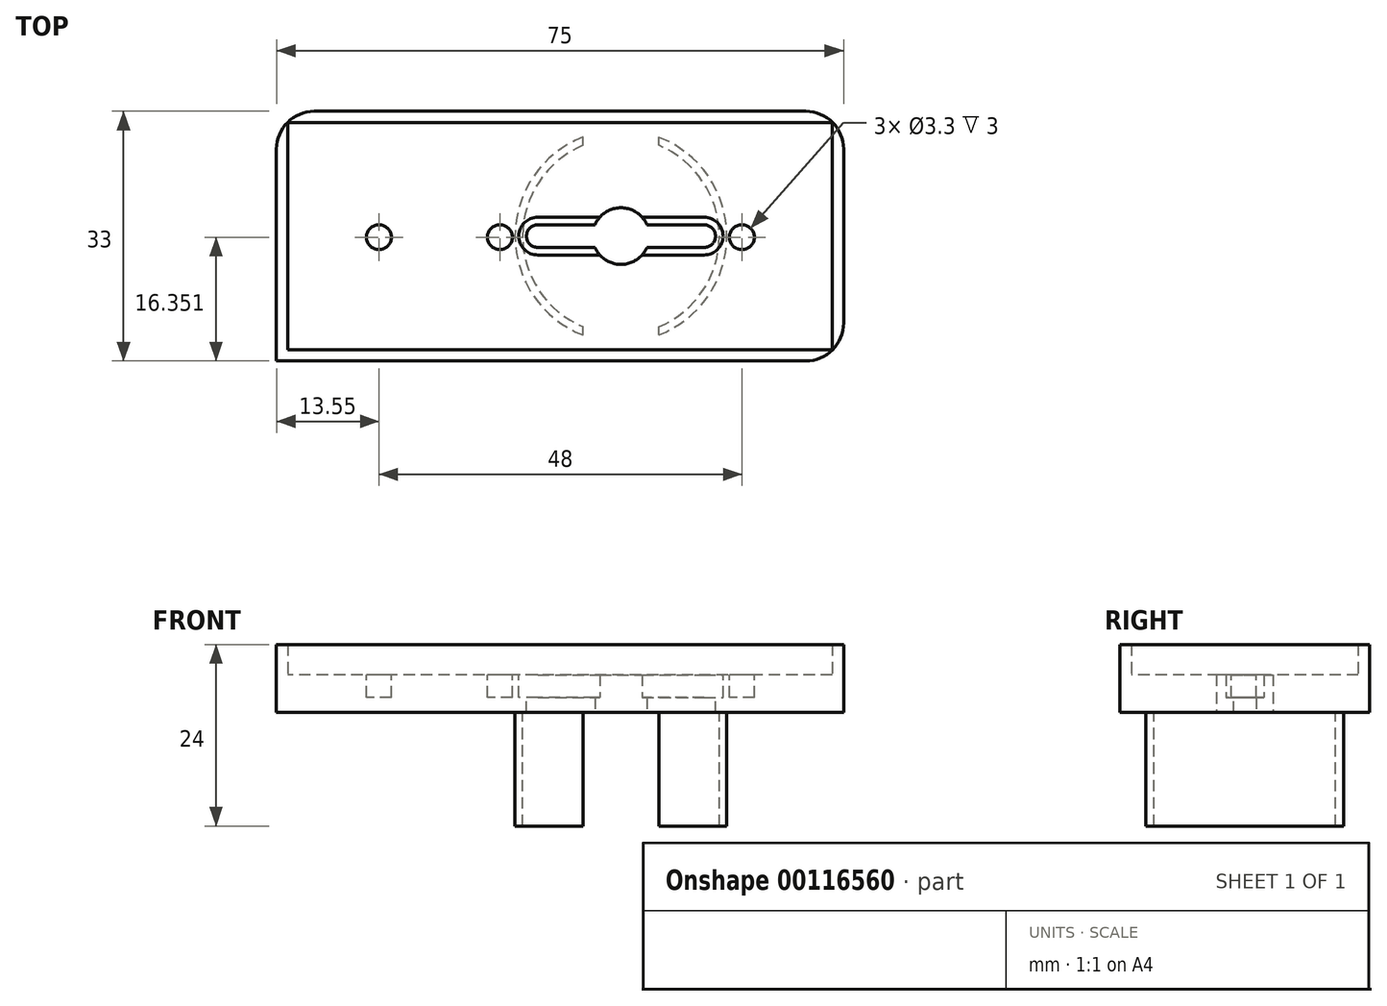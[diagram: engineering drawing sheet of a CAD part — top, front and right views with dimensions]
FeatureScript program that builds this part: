
annotation { "Feature Type Name" : "Feature", "Feature Type Description" : "" }
export const myFeature = defineFeature(function(context is Context, id is Id, definition is map)
    precondition{}
    {
        {
            var Q0;
            Q0=qCreatedBy(makeId("Top.planeOp"),FACE);
            var sketch = newSketch(context, id + "F0", { "sketchPlane" : qUnion([Q0])});
            skLineSegment(sketch, "E0.bottom", {"start": v(32.45, 18.12) * mm, "end": v(-32.55, 18.12) * mm});
            skLineSegment(sketch, "E0.top", {"start": v(32.45, -14.88) * mm, "end": v(-32.55, -14.88) * mm});
            skLineSegment(sketch, "E0.left", {"start": v(37.45, 13.12) * mm, "end": v(37.45, -9.88) * mm});
            skLineSegment(sketch, "E0.right", {"start": v(-37.55, 13.12) * mm, "end": v(-37.55, -9.88) * mm});
            skPoint(sketch, "E0.middle", {"position": v(-0.05, 1.62) * mm});
            skLineSegment(sketch, "E1.0", {"start": v(-36.05, 16.62) * mm, "end": v(-36.05, -13.38) * mm});
            skLineSegment(sketch, "E1.1", {"start": v(35.95, 16.62) * mm, "end": v(-36.05, 16.62) * mm});
            skLineSegment(sketch, "E1.2", {"start": v(35.95, 16.62) * mm, "end": v(35.95, -13.38) * mm});
            skLineSegment(sketch, "E1.3", {"start": v(35.95, -13.38) * mm, "end": v(-36.05, -13.38) * mm});
            skPoint(sketch, "E2.visualSharp", {"position": v(-37.55, -14.88) * mm});
            skPoint(sketch, "E3.visualSharp", {"position": v(37.45, -14.88) * mm});
            skArc(sketch, "E3.filletArc", {"start": v(32.45, -14.88) * mm, "mid": v(35.98, -13.42) * mm, "end": v(37.45, -9.88) * mm});
            skPoint(sketch, "E4.visualSharp", {"position": v(37.45, 18.12) * mm});
            skArc(sketch, "E4.filletArc", {"start": v(37.45, 13.12) * mm, "mid": v(35.98, 16.65) * mm, "end": v(32.45, 18.12) * mm});
            skPoint(sketch, "E5.visualSharp", {"position": v(-37.55, 18.12) * mm});
            skArc(sketch, "E5.filletArc", {"start": v(-32.55, 18.12) * mm, "mid": v(-36.09, 16.65) * mm, "end": v(-37.55, 13.12) * mm});
            skLineSegment(sketch, "E6", {"start": v(-32.55, -14.88) * mm, "end": v(-37.55, -14.88) * mm});
            skLineSegment(sketch, "E7", {"start": v(-37.55, -9.88) * mm, "end": v(-37.55, -14.88) * mm});
            skSolve(sketch);
        }
        {
            var Q0;
            Q0 = qSketchRegion(id + "F0", true);
            extrude(context, id + "F1", {"entities" : qUnion([Q0]), "depth" : 4 * mm});
        }
        {
            var Q0;
            Q0=makeQuery(id+"F1.opExtrude","CAP_FACE",FACE,{"disambiguationData":[OSD([sQuery(id+"F0.wireOp",EDGE,"E0.bottom"),sQuery(id+"F0.wireOp",EDGE,"E0.top"),sQuery(id+"F0.wireOp",EDGE,"E0.left"),sQuery(id+"F0.wireOp",EDGE,"E0.right"),sQuery(id+"F0.wireOp",EDGE,"E1.0"),sQuery(id+"F0.wireOp",EDGE,"E1.1"),sQuery(id+"F0.wireOp",EDGE,"E1.2"),sQuery(id+"F0.wireOp",EDGE,"E1.3"),sQuery(id+"F0.wireOp",EDGE,"E2.filletArc"),sQuery(id+"F0.wireOp",EDGE,"E3.filletArc"),sQuery(id+"F0.wireOp",EDGE,"E4.filletArc")])],"isStart":true});
            var sketch = newSketch(context, id + "F2", { "sketchPlane" : qUnion([Q0])});
            skLineSegment(sketch, "E8.bottom", {"start": v(-37.55, 14.88) * mm, "end": v(32.45, 14.88) * mm});
            skLineSegment(sketch, "E8.top", {"start": v(-32.55, -18.12) * mm, "end": v(32.45, -18.12) * mm});
            skLineSegment(sketch, "E8.left", {"start": v(-37.55, 14.88) * mm, "end": v(-37.55, -13.12) * mm});
            skLineSegment(sketch, "E8.right", {"start": v(37.45, 9.88) * mm, "end": v(37.45, -13.12) * mm});
            skPoint(sketch, "E9.visualSharp", {"position": v(-37.55, -18.12) * mm});
            skArc(sketch, "E9.filletArc", {"start": v(-37.55, -13.12) * mm, "mid": v(-36.09, -16.65) * mm, "end": v(-32.55, -18.12) * mm});
            skPoint(sketch, "E10.visualSharp", {"position": v(37.45, -18.12) * mm});
            skArc(sketch, "E10.filletArc", {"start": v(32.45, -18.12) * mm, "mid": v(35.98, -16.65) * mm, "end": v(37.45, -13.12) * mm});
            skPoint(sketch, "E11.visualSharp", {"position": v(37.45, 14.88) * mm});
            skArc(sketch, "E11.filletArc", {"start": v(37.45, 9.88) * mm, "mid": v(35.98, 13.42) * mm, "end": v(32.45, 14.88) * mm});
            skSolve(sketch);
        }
        {
            var Q0;
            Q0 = qSketchRegion(id + "F2", true);
            extrude(context, id + "F3", {"entities" : qUnion([Q0]), "operationType" : NewBodyOperationType.ADD, "depth" : 5 * mm});
        }
        {
            var Q0;
            Q0=makeQuery(id+"F3.opExtrude","CAP_FACE",FACE,{"disambiguationData":[OSD([sQuery(id+"F2.wireOp",EDGE,"E8.bottom"),sQuery(id+"F2.wireOp",EDGE,"E8.top"),sQuery(id+"F2.wireOp",EDGE,"E8.left"),sQuery(id+"F2.wireOp",EDGE,"E8.right"),sQuery(id+"F2.wireOp",EDGE,"E9.filletArc"),sQuery(id+"F2.wireOp",EDGE,"E10.filletArc"),sQuery(id+"F2.wireOp",EDGE,"E11.filletArc")])],"isStart":false});
            var sketch = newSketch(context, id + "F4", { "sketchPlane" : qUnion([Q0])});
            skLineSegment(sketch, "E12", {"start": v(0, 14.88) * mm, "end": v(8, 14.88) * mm, "construction": true});
            skLineSegment(sketch, "E13", {"start": v(8, 14.88) * mm, "end": v(8, -18.12) * mm, "construction": true});
            skPoint(sketch, "E14", {"position": v(8, -1.62) * mm});
            skCircle(sketch, "E15", {"center": v(8, -1.62) * mm, "radius": 3.75 * mm});
            skSolve(sketch);
        }
        {
            var Q0;
            Q0 = qSketchRegion(id + "F4", true);
            extrude(context, id + "F5", {"entities" : qUnion([Q0]), "operationType" : NewBodyOperationType.REMOVE, "endBound" : BoundingType.THROUGH_ALL, "oppositeDirection" : true, "depth" : 25 * mm});
        }
        {
            var Q0;
            Q0=makeQuery(id+"F3.opExtrude","CAP_FACE",FACE,{"disambiguationData":[OSD([sQuery(id+"F2.wireOp",EDGE,"E8.bottom"),sQuery(id+"F2.wireOp",EDGE,"E8.top"),sQuery(id+"F2.wireOp",EDGE,"E8.left"),sQuery(id+"F2.wireOp",EDGE,"E8.right"),sQuery(id+"F2.wireOp",EDGE,"E9.filletArc"),sQuery(id+"F2.wireOp",EDGE,"E10.filletArc"),sQuery(id+"F2.wireOp",EDGE,"E11.filletArc")])],"isStart":false});
            var sketch = newSketch(context, id + "F6", { "sketchPlane" : qUnion([Q0])});
            skCircle(sketch, "E16", {"center": v(8, -1.62) * mm, "radius": 10 * mm});
            skSolve(sketch);
        }
        {
            var Q0;
            Q0=makeQuery(id+"F3.opExtrude","CAP_FACE",FACE,{"disambiguationData":[OSD([sQuery(id+"F2.wireOp",EDGE,"E8.bottom"),sQuery(id+"F2.wireOp",EDGE,"E8.top"),sQuery(id+"F2.wireOp",EDGE,"E8.left"),sQuery(id+"F2.wireOp",EDGE,"E8.right"),sQuery(id+"F2.wireOp",EDGE,"E9.filletArc"),sQuery(id+"F2.wireOp",EDGE,"E10.filletArc"),sQuery(id+"F2.wireOp",EDGE,"E11.filletArc")])],"isStart":false});
            var sketch = newSketch(context, id + "F7", { "sketchPlane" : qUnion([Q0])});
            skArc(sketch, "E17", {"start": v(3, 10.38) * mm, "mid": v(-5, -1.62) * mm, "end": v(3, -13.61) * mm});
            skArc(sketch, "E18.0", {"start": v(3, 11.46) * mm, "mid": v(-6, -1.62) * mm, "end": v(3, -14.7) * mm});
            skLineSegment(sketch, "E19", {"start": v(3, 11.46) * mm, "end": v(3, 10.38) * mm});
            skLineSegment(sketch, "E20", {"start": v(8, -1.62) * mm, "end": v(8, -11.62) * mm, "construction": true});
            skLineSegment(sketch, "E21.MirrorCS", {"start": v(13, 11.46) * mm, "end": v(13, 10.38) * mm});
            skArc(sketch, "E22.trimOffspring", {"start": v(13, -13.61) * mm, "mid": v(21, -1.62) * mm, "end": v(13, 10.38) * mm});
            skArc(sketch, "E23.trimOffspring", {"start": v(13, -14.7) * mm, "mid": v(22, -1.62) * mm, "end": v(13, 11.46) * mm});
            skLineSegment(sketch, "E24.trimOffspring", {"start": v(3, -13.61) * mm, "end": v(3, -14.7) * mm});
            skLineSegment(sketch, "E25.trimOffspring", {"start": v(13, -13.61) * mm, "end": v(13, -14.7) * mm});
            skSolve(sketch);
        }
        {
            var Q0;
            Q0 = qSketchRegion(id + "F7", true);
            extrude(context, id + "F8", {"entities" : qUnion([Q0]), "operationType" : NewBodyOperationType.ADD, "depth" : 15 * mm});
        }
        {
            var Q0;
            Q0=makeQuery(id+"F3.opExtrude","CAP_FACE",FACE,{"disambiguationData":[OSD([sQuery(id+"F2.wireOp",EDGE,"E8.bottom"),sQuery(id+"F2.wireOp",EDGE,"E8.top"),sQuery(id+"F2.wireOp",EDGE,"E8.left"),sQuery(id+"F2.wireOp",EDGE,"E8.right"),sQuery(id+"F2.wireOp",EDGE,"E9.filletArc"),sQuery(id+"F2.wireOp",EDGE,"E10.filletArc"),sQuery(id+"F2.wireOp",EDGE,"E11.filletArc")])],"isStart":true});
            var sketch = newSketch(context, id + "F9", { "sketchPlane" : qUnion([Q0])});
            skLineSegment(sketch, "E26", {"start": v(8, 1.62) * mm, "end": v(19, 1.62) * mm, "construction": true});
            skCircle(sketch, "E27", {"center": v(19, 1.62) * mm, "radius": 1.5 * mm});
            skLineSegment(sketch, "E28", {"start": v(8, 1.62) * mm, "end": v(8, -10.57) * mm, "construction": true});
            skCircle(sketch, "E29.MirrorC", {"center": v(-3, 1.62) * mm, "radius": 1.5 * mm});
            skLineSegment(sketch, "E30", {"start": v(-3, 3.12) * mm, "end": v(19, 3.12) * mm});
            skLineSegment(sketch, "E31", {"start": v(-3, 0.12) * mm, "end": v(19, 0.12) * mm});
            skSolve(sketch);
        }
        {
            var Q0;
            Q0 = qSketchRegion(id + "F9", true);
            extrude(context, id + "F10", {"entities" : qUnion([Q0]), "operationType" : NewBodyOperationType.REMOVE, "oppositeDirection" : true, "depth" : 25 * mm});
        }
        {
            var Q0;
            Q0=makeQuery(id+"F3.opExtrude","CAP_FACE",FACE,{"disambiguationData":[OSD([sQuery(id+"F2.wireOp",EDGE,"E8.bottom"),sQuery(id+"F2.wireOp",EDGE,"E8.top"),sQuery(id+"F2.wireOp",EDGE,"E8.left"),sQuery(id+"F2.wireOp",EDGE,"E8.right"),sQuery(id+"F2.wireOp",EDGE,"E9.filletArc"),sQuery(id+"F2.wireOp",EDGE,"E10.filletArc"),sQuery(id+"F2.wireOp",EDGE,"E11.filletArc")])],"isStart":true});
            var sketch = newSketch(context, id + "F11", { "sketchPlane" : qUnion([Q0])});
            skCircle(sketch, "E32", {"center": v(-3, 1.62) * mm, "radius": 2.5 * mm});
            skLineSegment(sketch, "E33", {"start": v(8, 1.62) * mm, "end": v(8, -8.17) * mm, "construction": true});
            skCircle(sketch, "E34.MirrorC", {"center": v(19, 1.62) * mm, "radius": 2.5 * mm});
            skLineSegment(sketch, "E35", {"start": v(-3, 4.12) * mm, "end": v(19, 4.12) * mm});
            skLineSegment(sketch, "E36", {"start": v(-3, -0.88) * mm, "end": v(19, -0.88) * mm});
            skSolve(sketch);
        }
        {
            var Q0;
            Q0 = qSketchRegion(id + "F11", true);
            extrude(context, id + "F12", {"entities" : qUnion([Q0]), "operationType" : NewBodyOperationType.REMOVE, "oppositeDirection" : true, "depth" : 3 * mm});
        }
        {
            var Q0;
            Q0=makeQuery(id+"F3.opExtrude","CAP_FACE",FACE,{"disambiguationData":[OSD([sQuery(id+"F2.wireOp",EDGE,"E8.bottom"),sQuery(id+"F2.wireOp",EDGE,"E8.top"),sQuery(id+"F2.wireOp",EDGE,"E8.left"),sQuery(id+"F2.wireOp",EDGE,"E8.right"),sQuery(id+"F2.wireOp",EDGE,"E9.filletArc"),sQuery(id+"F2.wireOp",EDGE,"E10.filletArc"),sQuery(id+"F2.wireOp",EDGE,"E11.filletArc")])],"isStart":true});
            var sketch = newSketch(context, id + "F13", { "sketchPlane" : qUnion([Q0])});
            skCircle(sketch, "E37", {"center": v(-24, 1.47) * mm, "radius": 1.65 * mm});
            skCircle(sketch, "E38.1.0.0", {"center": v(-8, 1.47) * mm, "radius": 1.65 * mm});
            skCircle(sketch, "E38.2.0.0", {"center": v(8, 1.47) * mm, "radius": 1.65 * mm});
            skCircle(sketch, "E38.3.0.0", {"center": v(24, 1.47) * mm, "radius": 1.65 * mm});
            skLineSegment(sketch, "E38.direction1", {"start": v(-24, 1.47) * mm, "end": v(-8, 1.47) * mm, "construction": true});
            skSolve(sketch);
        }
        {
            var Q0;
            Q0 = qSketchRegion(id + "F13", true);
            extrude(context, id + "F14", {"entities" : qUnion([Q0]), "operationType" : NewBodyOperationType.REMOVE, "oppositeDirection" : true, "depth" : 3 * mm});
        }
    });
